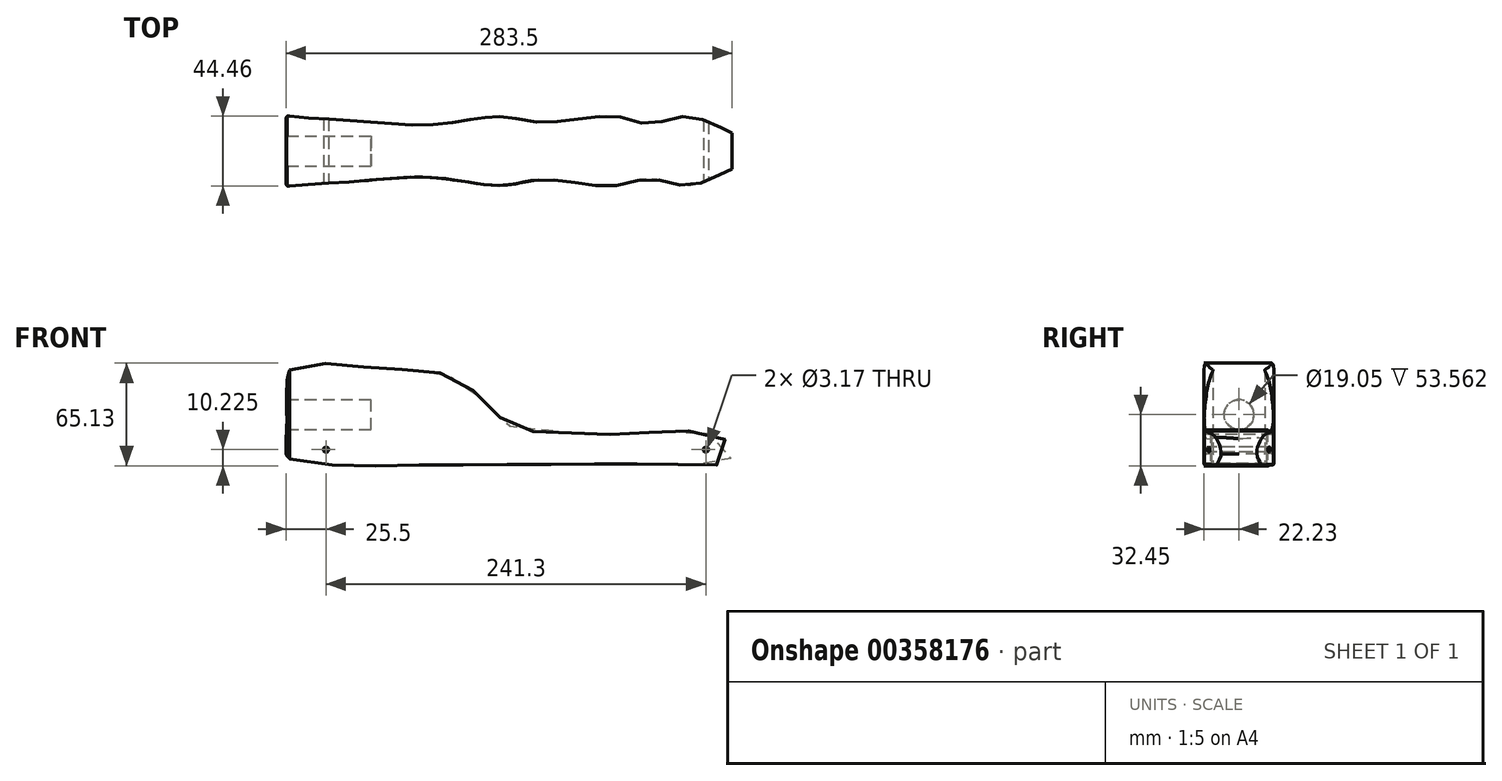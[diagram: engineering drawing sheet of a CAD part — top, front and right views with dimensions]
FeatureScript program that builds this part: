
annotation { "Feature Type Name" : "Feature", "Feature Type Description" : "" }
export const myFeature = defineFeature(function(context is Context, id is Id, definition is map)
    precondition{}
    {
        {
            var Q0;
            Q0=qCreatedBy(makeId("Front.planeOp"),FACE);
            var sketch = newSketch(context, id + "F0", { "sketchPlane" : qUnion([Q0])});
            skLineSegment(sketch, "E0.bottom", {"start": v(-146.05, 31.75) * mm, "end": v(146.05, 31.75) * mm, "construction": true});
            skLineSegment(sketch, "E0.top", {"start": v(-146.05, -31.75) * mm, "end": v(146.05, -31.75) * mm, "construction": true});
            skLineSegment(sketch, "E0.right", {"start": v(146.05, 31.75) * mm, "end": v(146.05, -31.75) * mm, "construction": true});
            skFitSpline(sketch, "E1", {"points": [v(-145.98, -14.44) * mm, v(-145.57, 3.4) * mm, v(-144.1, 27.37) * mm, v(-139.3, 31.56) * mm, v(-123.91, 32.6) * mm, v(-106.86, 30.98) * mm, v(-71.7, 28.8) * mm, v(-33.5, 20.24) * mm, v(0, -9.52) * mm, v(17.64, -9.9) * mm, v(36.27, -11.77) * mm, v(70.95, -12.08) * mm, v(111.85, -10.49) * mm, v(122.51, -11.8) * mm, v(129.82, -14.32) * mm, v(136.2, -19.4) * mm, v(136.76, -27.21) * mm, v(131.84, -31.75) * mm, v(123.86, -31.75) * mm, v(112.86, -31.75) * mm, v(89.1, -31.17) * mm, v(67.42, -31.44) * mm, v(44.74, -31.43) * mm, v(17.54, -31.7) * mm, v(-8.95, -31.75) * mm, v(-29.72, -31.86) * mm, v(-61.1, -31.84) * mm, v(-92.6, -32.45) * mm, v(-112.12, -32.04) * mm, v(-137.9, -30.76) * mm, v(-146.05, -24.85) * mm, v(-145.98, -14.44) * mm]});
            skLineSegment(sketch, "E2.bottom", {"start": v(-146.05, 9.52) * mm, "end": v(-95.25, 9.52) * mm, "construction": true});
            skLineSegment(sketch, "E2.top", {"start": v(-141.83, -9.52) * mm, "end": v(-95.25, -9.52) * mm, "construction": true});
            skLineSegment(sketch, "E2.right", {"start": v(-95.25, 9.52) * mm, "end": v(-95.25, -9.52) * mm, "construction": true});
            skLineSegment(sketch, "E3", {"start": v(-146.05, 31.75) * mm, "end": v(-146.05, -31.75) * mm, "construction": true});
            skSolve(sketch);
        }
        {
            var Q0;
            Q0=qCreatedBy(makeId("Top.planeOp"),FACE);
            var sketch = newSketch(context, id + "F1", { "sketchPlane" : qUnion([Q0])});
            skLineSegment(sketch, "E4.bottom", {"start": v(-146.05, 22.22) * mm, "end": v(146.05, 22.23) * mm, "construction": true});
            skLineSegment(sketch, "E4.top", {"start": v(-146.05, -22.23) * mm, "end": v(146.05, -22.22) * mm, "construction": true});
            skLineSegment(sketch, "E4.left", {"start": v(-146.05, 22.22) * mm, "end": v(-146.05, -22.23) * mm, "construction": true});
            skLineSegment(sketch, "E4.right", {"start": v(146.05, 22.22) * mm, "end": v(146.05, -22.22) * mm, "construction": true});
            skLineSegment(sketch, "E5", {"start": v(-146.05, 0) * mm, "end": v(146.05, 0) * mm, "construction": true});
            skFitSpline(sketch, "E6", {"points": [v(-146.05, 0) * mm, v(-146.05, 16.22) * mm, v(-145.68, 21.83) * mm, v(-141.76, 21.98) * mm, v(-96.68, 18.84) * mm, v(-50.26, 16.97) * mm, v(-8.22, 21.87) * mm, v(16.23, 18.2) * mm, v(62.6, 21.96) * mm, v(84.93, 17.44) * mm, v(109.9, 22) * mm, v(128.35, 15.47) * mm, v(134.37, 13.38) * mm, v(138.67, 10.34) * mm, v(146.05, 0) * mm], "startDerivative": vector(0, 335.54) * mm, "endDerivative": vector(0, -277.49) * mm});
            skFitSpline(sketch, "E7.MirrorCS", {"points": [v(-146.05, 0) * mm, v(-146.05, -16.22) * mm, v(-145.68, -21.83) * mm, v(-141.76, -21.98) * mm, v(-96.68, -18.84) * mm, v(-50.26, -16.97) * mm, v(-8.22, -21.87) * mm, v(16.23, -18.2) * mm, v(62.6, -21.96) * mm, v(84.93, -17.44) * mm, v(109.9, -22) * mm, v(128.35, -15.47) * mm, v(134.37, -13.38) * mm, v(138.67, -10.34) * mm, v(146.05, 0) * mm], "startDerivative": vector(0, -335.54) * mm, "endDerivative": vector(0, 277.49) * mm});
            skLineSegment(sketch, "E8.MirrorCS", {"start": v(-146.05, -22.23) * mm, "end": v(146.05, -22.23) * mm});
            skSolve(sketch);
        }
        {
            var Q0;
            Q0=qCreatedBy(makeId("Right.planeOp"),FACE);
            var sketch = newSketch(context, id + "F2", { "sketchPlane" : qUnion([Q0])});
            skCircle(sketch, "E9", {"center": v(0, 0) * mm, "radius": 9.53 * mm});
            skSolve(sketch);
        }
        {
            var Q0;
            Q0=qCreatedBy(makeId("Front.planeOp"),FACE);
            var sketch = newSketch(context, id + "F3", { "sketchPlane" : qUnion([Q0])});
            skCircle(sketch, "E10", {"center": v(-120.65, -22.22) * mm, "radius": 1.59 * mm});
            skCircle(sketch, "E11", {"center": v(120.65, -22.23) * mm, "radius": 1.59 * mm});
            skSolve(sketch);
        }
        {
            var Q0;
            Q0=qSketchRegion(id+"F0",true);
            extrude(context, id + "F4", {"entities" : qUnion([Q0]), "depth" : 44.45 * mm, "symmetric" : true});
        }
        {
            var Q0;
            Q0=qSketchRegion(id+"F1",true);
            extrude(context, id + "F5", {"entities" : qUnion([Q0]), "operationType" : NewBodyOperationType.INTERSECT, "endBound" : BoundingType.THROUGH_ALL, "oppositeDirection" : true, "depth" : 60.96 * mm, "hasSecondDirection" : true, "secondDirectionBound" : BoundingType.THROUGH_ALL, "secondDirectionOppositeDirection" : false, "secondDirectionDepth" : 25.4 * mm});
        }
        {
            var Q0;
            Q0=qSketchRegion(id+"F2",true);
            extrude(context, id + "F6", {"entities" : qUnion([Q0]), "operationType" : NewBodyOperationType.REMOVE, "oppositeDirection" : true, "depth" : 152.4 * mm, "hasSecondDirection" : true, "secondDirectionOppositeDirection" : true, "secondDirectionDepth" : 92.07 * mm});
        }
        {
            var Q0;
            Q0=qSketchRegion(id+"F3",true);
            extrude(context, id + "F7", {"entities" : qUnion([Q0]), "operationType" : NewBodyOperationType.REMOVE, "oppositeDirection" : true, "depth" : 50.8 * mm, "symmetric" : true});
        }
    });
